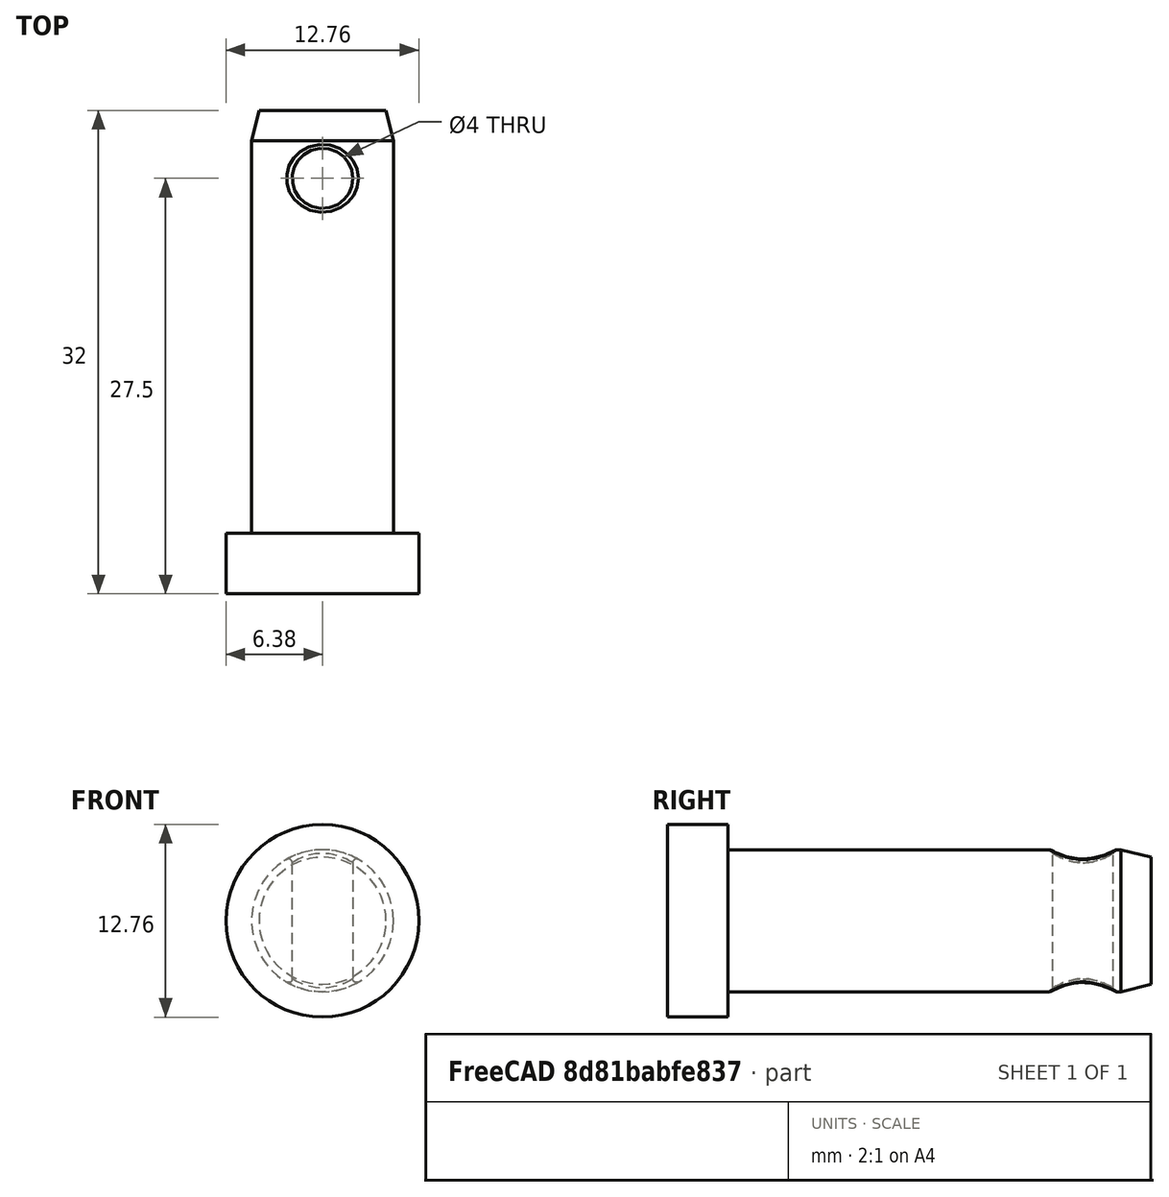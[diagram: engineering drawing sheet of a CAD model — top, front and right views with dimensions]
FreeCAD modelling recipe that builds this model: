
FCSTD DOCUMENT  (FreeCAD 0.19R22319 (Git))
Label: Lawn Mower Deck Pin
License: Creative Commons Attribution
LicenseURL: http://creativecommons.org/licenses/by/4.0/
objects: Sketcher::SketchObject×2, PartDesign::Revolution×1, PartDesign::Pocket×1, PartDesign::Fillet×1, PartDesign::Body×1, Mesh::Feature×1
note: 9 computed .brp shape members not serialized (recipe doc carries the construction recipe); baked Part::Feature solids carry a one-line shape summary decoded from their .brp

FEATURE [Sketcher::SketchObject] Sketch
  MapMode = 5
  Support = -> [XY_Plane]
  expr: Constraints[12] = 12.75 / 2
  expr: Constraints[5] = 9.4 / 2 - 0.5
  expr: Constraints[3] = 9.4 / 2
  sketch-geometry (7):
    g0: LineSegment StartX=4.7 StartY=0 StartZ=0 EndX=4.7 EndY=26 EndZ=0
    g1: LineSegment StartX=4.7 StartY=26 StartZ=0 EndX=4.2 EndY=28 EndZ=0
    g2: LineSegment StartX=4.2 StartY=28 StartZ=0 EndX=0 EndY=28 EndZ=0
    g3: LineSegment StartX=4.7 StartY=0 StartZ=0 EndX=6.375 EndY=0 EndZ=0
    g4: LineSegment StartX=6.375 StartY=0 StartZ=0 EndX=6.375 EndY=-4 EndZ=0
    g5: LineSegment StartX=6.375 StartY=-4 StartZ=0 EndX=0 EndY=-4 EndZ=0
    g6: LineSegment StartX=0 StartY=28 StartZ=0 EndX=0 EndY=-4 EndZ=0
  constraints (21):
    c: PointOnObject(g0,g-1)
    c: Vertical(g0)
    c: Distance(g0) = 26
    c: DistanceX(g-1,g0) = 4.7
    c: Coincident(g1,g0)
    c: DistanceX(g-1,g1) = 4.2
    c: Coincident(g2,g1)
    c: PointOnObject(g2,g-2)
    c: Horizontal(g2)
    c: DistanceY(g-1,g1) = 28
    c: Coincident(g3,g0)
    c: PointOnObject(g3,g-1)
    c: DistanceX(g-1,g3) = 6.375
    c: Coincident(g4,g3)
    c: Vertical(g4)
    c: Coincident(g5,g4)
    c: PointOnObject(g5,g-2)
    c: Horizontal(g5)
    c: Distance(g4) = 4
    c: Coincident(g6,g2)
    c: Coincident(g6,g5)
FEATURE [PartDesign::Revolution] Revolution
  Angle = 360
  Axis = (0,1,0)
  Base = (0,0,0)
  Profile = -> Sketch
  ReferenceAxis = -> Sketch [V_Axis]
FEATURE [Sketcher::SketchObject] Sketch001
  AttachmentOffset = pos=(0,0,5) rot=(0,0,1;0rad)
  ExternalGeometry = -> [Revolution]
  MapMode = 5
  Placement = pos=(0,0,5) rot=(0,0,1;0rad)
  Support = -> [XY_Plane]
  expr: Constraints[2] = 2.5 + 2
  sketch-geometry (1):
    g0: Circle CenterX=0 CenterY=23.5 CenterZ=0 NormalX=0 NormalY=0 NormalZ=1 AngleXU=0 Radius=2
  constraints (3):
    c: PointOnObject(g0,g-2)
    c: Radius(g0) = 2
    c: Distance(g0,g-3) = 4.5
FEATURE [PartDesign::Pocket] Pocket
  BaseFeature = -> Revolution
  Length = 11
  Length2 = 100
  Profile = -> Sketch001
  Type = 0
FEATURE [PartDesign::Fillet] Fillet
  Base = -> Pocket [Edge4,Edge5]
  BaseFeature = -> Pocket
  Radius = 0.25
  SupportTransform = false
FEATURE [PartDesign::Body] Body
  Group = -> [Sketch,Revolution,Sketch001,Pocket,Fillet]
  Origin = -> Origin
  Tip = -> Fillet
FEATURE [Mesh::Feature] Mesh  label="Body (Meshed)"
